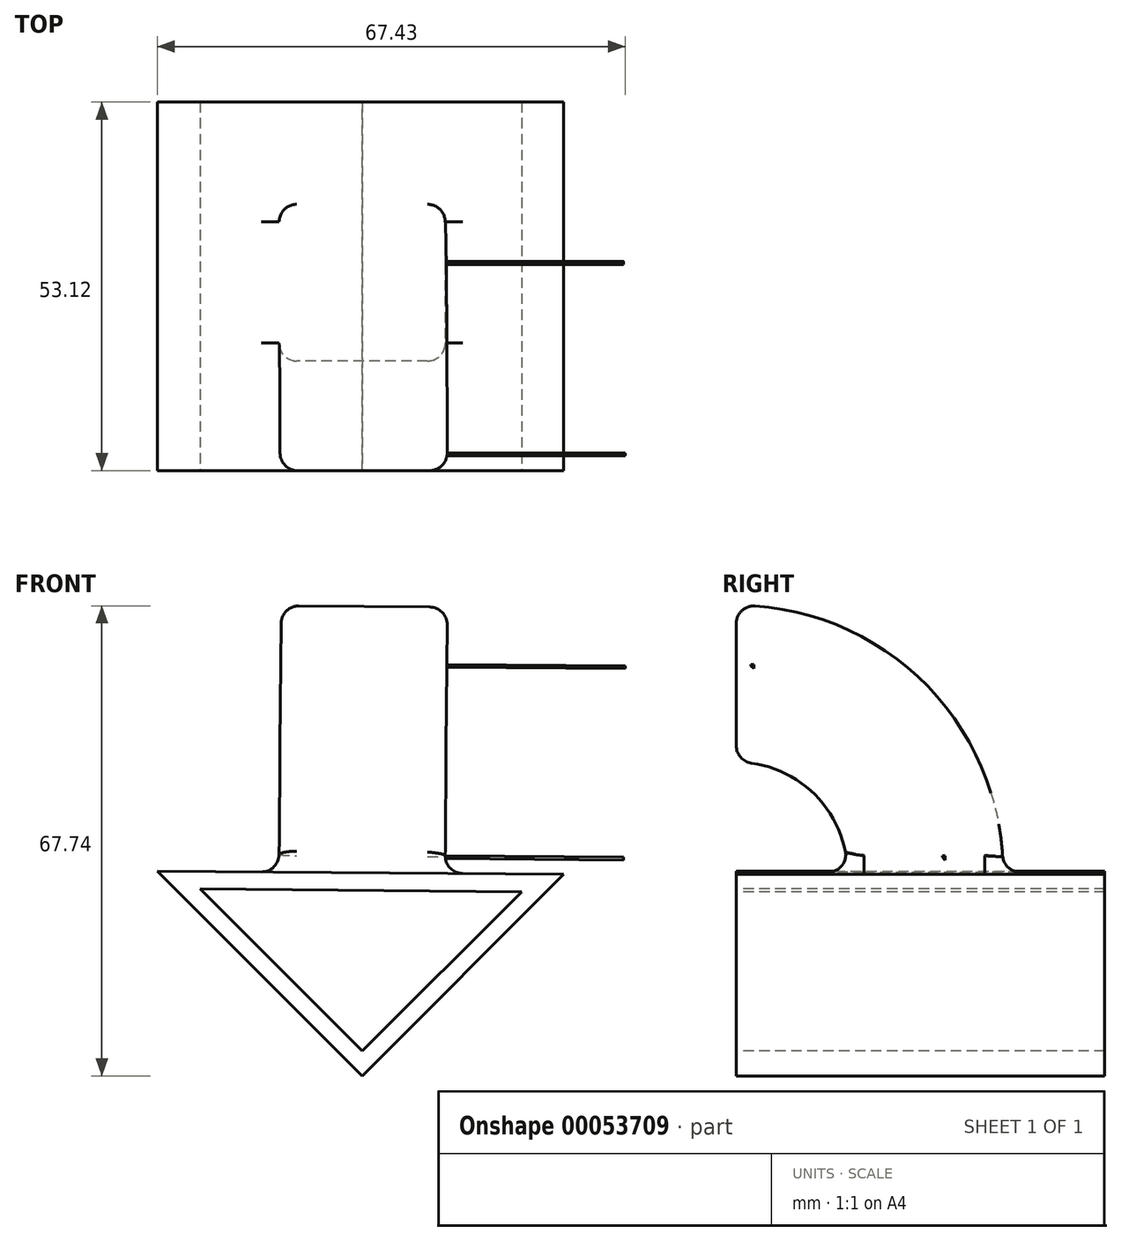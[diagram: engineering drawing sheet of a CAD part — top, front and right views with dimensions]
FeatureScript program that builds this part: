
annotation { "Feature Type Name" : "Feature", "Feature Type Description" : "" }
export const myFeature = defineFeature(function(context is Context, id is Id, definition is map)
    precondition{}
    {
        {
            var Q0;
            Q0=qCreatedBy(makeId("Front.planeOp"),FACE);
            var sketch = newSketch(context, id + "F0", { "sketchPlane" : qUnion([Q0])});
            skLineSegment(sketch, "E0", {"start": v(-29.52, 29.53) * mm, "end": v(0, 0) * mm});
            skLineSegment(sketch, "E1", {"start": v(0, 0) * mm, "end": v(29.05, 29.04) * mm});
            skLineSegment(sketch, "E2", {"start": v(29.05, 29.04) * mm, "end": v(-29.52, 29.53) * mm});
            skSolve(sketch);
        }
        {
            var Q0;
            Q0=makeQuery(id+"F0.imprint","IMPRINT",FACE,{"disambiguationData":[TD([[makeQuery(id+"F0.imprint","IMPRINT",EDGE,{"derivedFrom":sQuery(id+"F0.wireOp",EDGE,"E0")}),1.0]])]});
            extrude(context, id + "F1", {"entities" : qUnion([Q0]), "depth" : 53.12 * mm});
        }
        {
            var Q0;
            Q0=makeQuery(id+"F1.opExtrude","SWEPT_FACE",FACE,{"disambiguationData":[OSD([sQuery(id+"F0.wireOp",EDGE,"E2")])]});
            var sketch = newSketch(context, id + "F2", { "sketchPlane" : qUnion([Q0])});
            skLineSegment(sketch, "E3.bottom", {"start": v(-12.24, -14.66) * mm, "end": v(11.7, -14.66) * mm});
            skLineSegment(sketch, "E3.top", {"start": v(-12.24, -37.09) * mm, "end": v(11.7, -37.09) * mm});
            skLineSegment(sketch, "E3.left", {"start": v(-12.24, -14.66) * mm, "end": v(-12.24, -37.09) * mm});
            skLineSegment(sketch, "E3.right", {"start": v(11.7, -14.66) * mm, "end": v(11.7, -37.09) * mm});
            skSolve(sketch);
        }
        {
            var Q0;
            Q0=makeQuery(id+"F2.imprint","IMPRINT",FACE,{"disambiguationData":[TD([[makeQuery(id+"F2.imprint","IMPRINT",EDGE,{"derivedFrom":sQuery(id+"F2.wireOp",EDGE,"E3.bottom")}),-1.0]])]});
            var Q1;
            Q1=makeQuery(id+"F1.opExtrude","CAP_EDGE",EDGE,{"disambiguationData":[OSD([sQuery(id+"F0.wireOp",EDGE,"E2")])],"isStart":false});
            revolve(context, id + "F3", {"operationType" : NewBodyOperationType.ADD, "entities" : qUnion([Q0]), "axis" : qUnion([Q1]), "revolveType" : RevolveType.ONE_DIRECTION, "oppositeDirection" : true, "angle" : 90 * degree});
        }
        {
            var Q0;
            Q0=makeQuery(id+"F3.opRevolve","SWEPT_FACE",FACE,{"disambiguationData":[OSD([sQuery(id+"F2.wireOp",EDGE,"E3.right")])]});
            var Q1;
            Q1=makeQuery(id+"F3.opRevolve","CAP_FACE",FACE,{"disambiguationData":[OSD([sQuery(id+"F2.wireOp",EDGE,"E3.bottom"),sQuery(id+"F2.wireOp",EDGE,"E3.top"),sQuery(id+"F2.wireOp",EDGE,"E3.left"),sQuery(id+"F2.wireOp",EDGE,"E3.right")])],"isStart":false});
            var Q2;
            Q2=makeQuery(id+"F3.opRevolve","SWEPT_FACE",FACE,{"disambiguationData":[OSD([sQuery(id+"F2.wireOp",EDGE,"E3.bottom")])]});
            var Q3;
            Q3=makeQuery(id+"F3.opRevolve","SWEPT_FACE",FACE,{"disambiguationData":[OSD([sQuery(id+"F2.wireOp",EDGE,"E3.top")])]});
            var Q4;
            Q4=makeQuery(id+"F3.opRevolve","SWEPT_FACE",FACE,{"disambiguationData":[OSD([sQuery(id+"F2.wireOp",EDGE,"E3.left")])]});
            fillet(context, id + "F4", {"entities" : qUnion([Q0, Q1, Q2, Q3, Q4]), "radius" : 2.54 * mm, "tangentPropagation" : true, "allowEdgeOverflow" : false});
        }
        {
            var Q0;
            Q0=makeQuery(id+"F1.opExtrude","CAP_FACE",FACE,{"disambiguationData":[OSD([sQuery(id+"F0.wireOp",EDGE,"E0"),sQuery(id+"F0.wireOp",EDGE,"E1"),sQuery(id+"F0.wireOp",EDGE,"E2")])],"isStart":false});
            var sketch = newSketch(context, id + "F5", { "sketchPlane" : qUnion([Q0])});
            skLineSegment(sketch, "E4.0", {"start": v(22.97, 26.55) * mm, "end": v(-23.34, 26.94) * mm});
            skLineSegment(sketch, "E4.1", {"start": v(0, 3.6) * mm, "end": v(22.97, 26.55) * mm});
            skLineSegment(sketch, "E4.2", {"start": v(-23.34, 26.94) * mm, "end": v(0, 3.6) * mm});
            skSolve(sketch);
        }
        {
            var Q0;
            Q0=makeQuery(id+"F5.imprint","IMPRINT",FACE,{"disambiguationData":[TD([[makeQuery(id+"F5.imprint","IMPRINT",EDGE,{"derivedFrom":sQuery(id+"F5.wireOp",EDGE,"E4.0")}),1.0]])]});
            extrude(context, id + "F6", {"entities" : qUnion([Q0]), "operationType" : NewBodyOperationType.REMOVE, "endBound" : BoundingType.THROUGH_ALL, "oppositeDirection" : true, "depth" : 25.4 * mm});
        }
        {
            var Q0;
            Q0=makeQuery(id+"F3.opRevolve","SWEPT_FACE",FACE,{"disambiguationData":[OSD([sQuery(id+"F2.wireOp",EDGE,"E3.right")])]});
            var sketch = newSketch(context, id + "F7", { "sketchPlane" : qUnion([Q0])});
            skArc(sketch, "E5.0", {"start": v(-23, 31.42) * mm, "mid": v(-31.76, 50.64) * mm, "end": v(-50.99, 59.41) * mm});
            skLineSegment(sketch, "E6", {"start": v(-50.99, 59.41) * mm, "end": v(-23, 31.42) * mm});
            skSolve(sketch);
        }
        {
            var Q0;
            {var subQ0=sQuery(id+"F7.wireOp",EDGE,"E5.0");var subQ1=sQuery(id+"F2.wireOp",EDGE,"E3.right");var subQ2=makeQuery(id+"F3.opRevolve","SWEPT_FACE",FACE,{"disambiguationData":[OSD([subQ1])]});var subQ3=makeQuery(id+"F4.opFillet","BLEND_EDGE",EDGE,{"blendedFrom":[makeQuery(id+"F3.opRevolve","CAP_EDGE",EDGE,{"disambiguationData":[OSD([subQ1])],"isStart":true}),subQ2],"blendedInto":[subQ2]});var subQ4=makeQuery(id+"F7.imprint","INTERSECT",VERTEX,{"derivedFrom":[subQ3,subQ0]});Q0=makeQuery(id+"F7.imprint","IMPRINT",FACE,{"disambiguationData":[TD([[makeQuery(id+"F7.imprint","IMPRINT",EDGE,{"disambiguationData":[TD([[subQ4,-1.0]])],"derivedFrom":subQ0}),1.0]])]});}
            extrude(context, id + "F8", {"entities" : qUnion([Q0]), "operationType" : NewBodyOperationType.ADD, "depth" : 25.72 * mm});
        }
    });
